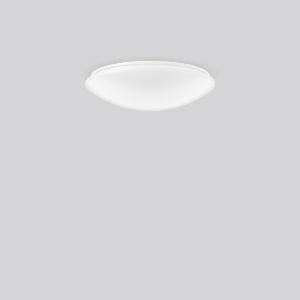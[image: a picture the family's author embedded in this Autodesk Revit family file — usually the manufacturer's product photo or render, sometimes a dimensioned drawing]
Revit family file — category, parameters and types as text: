
# Revit family: flat_polymero_672056_002_8_89_3421
name_source: partatom
category: Lighting Fixtures
units: mm (PartAtom-declared; Revit-internal decimal feet)

## family parameters
Cut with Voids When Loaded = No
Host = Face
Light Source = No
Part Type = Normal
Room Calculation Point = No
Round Connector Dimension = Use Diameter
Shared = No

## types (1)
- FLAT POLYMERO (1 x LED Modul 830, 1650 lm, 3000)
    Apparent Load = 15 VA
    CIE Flux Codes = 44 73 91 92 100
    Color Rendering = 80
    Color Temperature = 3000
    Default Elevation = 1800 mm
    Description = Series: FLAT POLYMERO
Decorative round surface-mounted luminaire. For escape route illumination. Base: metal, powder-coated. Diffuser made of plastic (polycarbonate), opal, shockproof. Diffuser fastening: patented push system. Suitable for Ceiling mounting, Wall (surface). Driver integrated. Suitable for connection to central battery systems. With AC Control monitoring module for LUXIFAIR central battery units. 
Colour: white
Diameter: 360 mm
Height: 100 mm
Weight: 1.34 kg
Operating mode: maintained power mode
Lamp: LED
Socket: without socket
Colour temperature: 3000K
Colour rendering index (CRI): 80
System power: 15 W
Rated luminous flux: 1650 lm
Luminous flux, emergency: 1650 lm
System power, emergency: 15 W
Control gear: Regulated power supply
Protection class: I
Type of protection: IP 40
    Height = 100 mm  [stored 0.328084 ft]
    Lamp = 1 x LED Modul 830
    Lamp Light Flux = 1650 lm
    Lamp count = 1
    Length = 360 mm
    Lifetime = 50000 h
    Luminous efficacy = 110 lm/W
    Manufacturer = RZB
    ModVariant = No
    Model = 672056.002.8.89
    Mounting Place = Ceiling
    Mounting Type = Surface mounted
    Number of Poles = 1
    OnlyDefault = Yes
    Power Factor = 1
    Product Name = FLAT POLYMERO
    Product group = Surface mounted ceiling and wall luminaires
    ProductGroupID = 305
    Protection Class = Protection class I
    Protection Degree = Degree of protection
    RLX_Detail_Level = 1
    RLX_Emergency_Light_Flux = 0 lm
    RLX_Emergency_Type = 0
    RLX_Emergency_Type_DB = No
    RlxData = <blob elided: 76357 chars, md5=5bd1b329>
    Socket = socket
    Standby Power = 0 W
    System Light Flux = 1650 lm
    System Power = 15 W
    Type Comments = ALEA SPOT
    Type Image = 311523.002.1.jpg
    URL = http://relux.com
    VarID = ---
    Voltage = 0 V
    Weight = 0.00 kg
    Width = 0 mm  [stored 0 ft]

note: [stored X ft] marks values corroborated as IEEE doubles in the binary element streams (Revit-internal decimal feet)

## geometry (parser evidence)
native form markers: Blend x4, Sweep x12
no freeform markers — native parametric forms only
